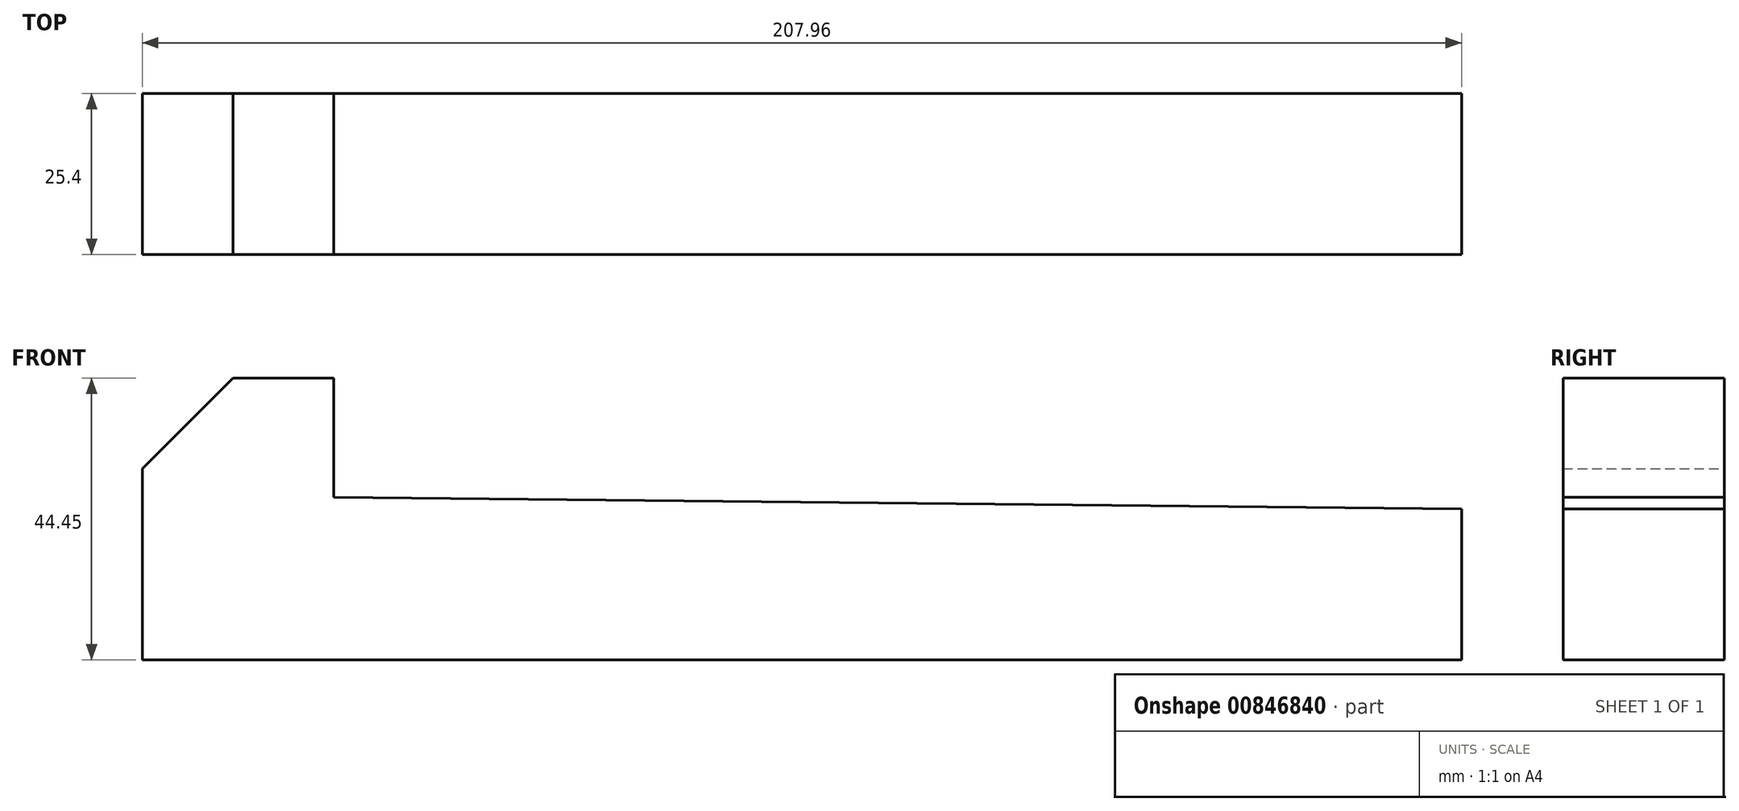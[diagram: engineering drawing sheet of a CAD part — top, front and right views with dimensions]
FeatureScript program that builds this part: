
annotation { "Feature Type Name" : "Feature", "Feature Type Description" : "" }
export const myFeature = defineFeature(function(context is Context, id is Id, definition is map)
    precondition{}
    {
        {
            var Q0;
            Q0=qCreatedBy(makeId("Front.planeOp"),FACE);
            var sketch = newSketch(context, id + "F0", { "sketchPlane" : qUnion([Q0])});
            skLineSegment(sketch, "E0", {"start": v(103.98, 0) * mm, "end": v(-103.98, 0) * mm});
            skLineSegment(sketch, "E1", {"start": v(-103.98, 0) * mm, "end": v(-103.98, 30.16) * mm});
            skLineSegment(sketch, "E2", {"start": v(-89.7, 44.45) * mm, "end": v(-73.82, 44.45) * mm});
            skLineSegment(sketch, "E3", {"start": v(-73.82, 44.45) * mm, "end": v(-73.82, 25.66) * mm});
            skLineSegment(sketch, "E4", {"start": v(-73.82, 25.66) * mm, "end": v(103.98, 23.81) * mm});
            skLineSegment(sketch, "E5", {"start": v(103.98, 0) * mm, "end": v(103.98, 23.81) * mm});
            skLineSegment(sketch, "E6", {"start": v(-103.98, 30.16) * mm, "end": v(-89.7, 44.45) * mm});
            skLineSegment(sketch, "E7", {"start": v(-48.42, 25.4) * mm, "end": v(-48.42, 0) * mm, "construction": true});
            skSolve(sketch);
        }
        {
            var Q0;
            Q0 = qSketchRegion(id + "F0", true);
            extrude(context, id + "F1", {"entities" : qUnion([Q0]), "depth" : 25.4 * mm, "offsetDistance" : 25.4 * mm, "symmetric" : true});
        }
    });
